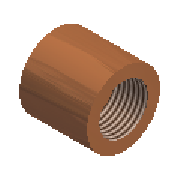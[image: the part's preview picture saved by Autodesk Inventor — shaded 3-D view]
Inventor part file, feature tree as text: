
AUTODESK INVENTOR PART (.ipt)
format: ipt  version: 2023.2 (Build 272271030, 271C)  size: 170,496 bytes
history: native  units: mm (DEFAULTED — no unit token found)
features: other x6, revolve x1, thread x1, sketch x1
ambient origin geometry x8: Origin, YZ Plane, XZ Plane, XY Plane, X Axis, Y Axis, Z Axis, Center Point
bodies: Solid1 (feature_tree)
feature tree (9):
  revolve  "Revolution1"  [1 undecoded]
  thread  "Thread1"  [1 undecoded]
  other  "Work Axis1"
  other  "Work Point1"
  other  "Work Point2"
  other  "Work Axis2"
  other  "Work Point3"
  other  "Work Point4"
  sketch  "Sketch1"  dims[d0=28.6258mm d1=13.716mm d2=24.638mm d7=90.0deg d3=0.312398mm d4=12.7mm d5=18.320766mm d12=25.4mm d13=0.0mm]
note: 2 required parameter values undecoded (feature->parameter linkage not recoverable at this tier; creation-order binding heuristic only, values carry confidence <= 0.55)